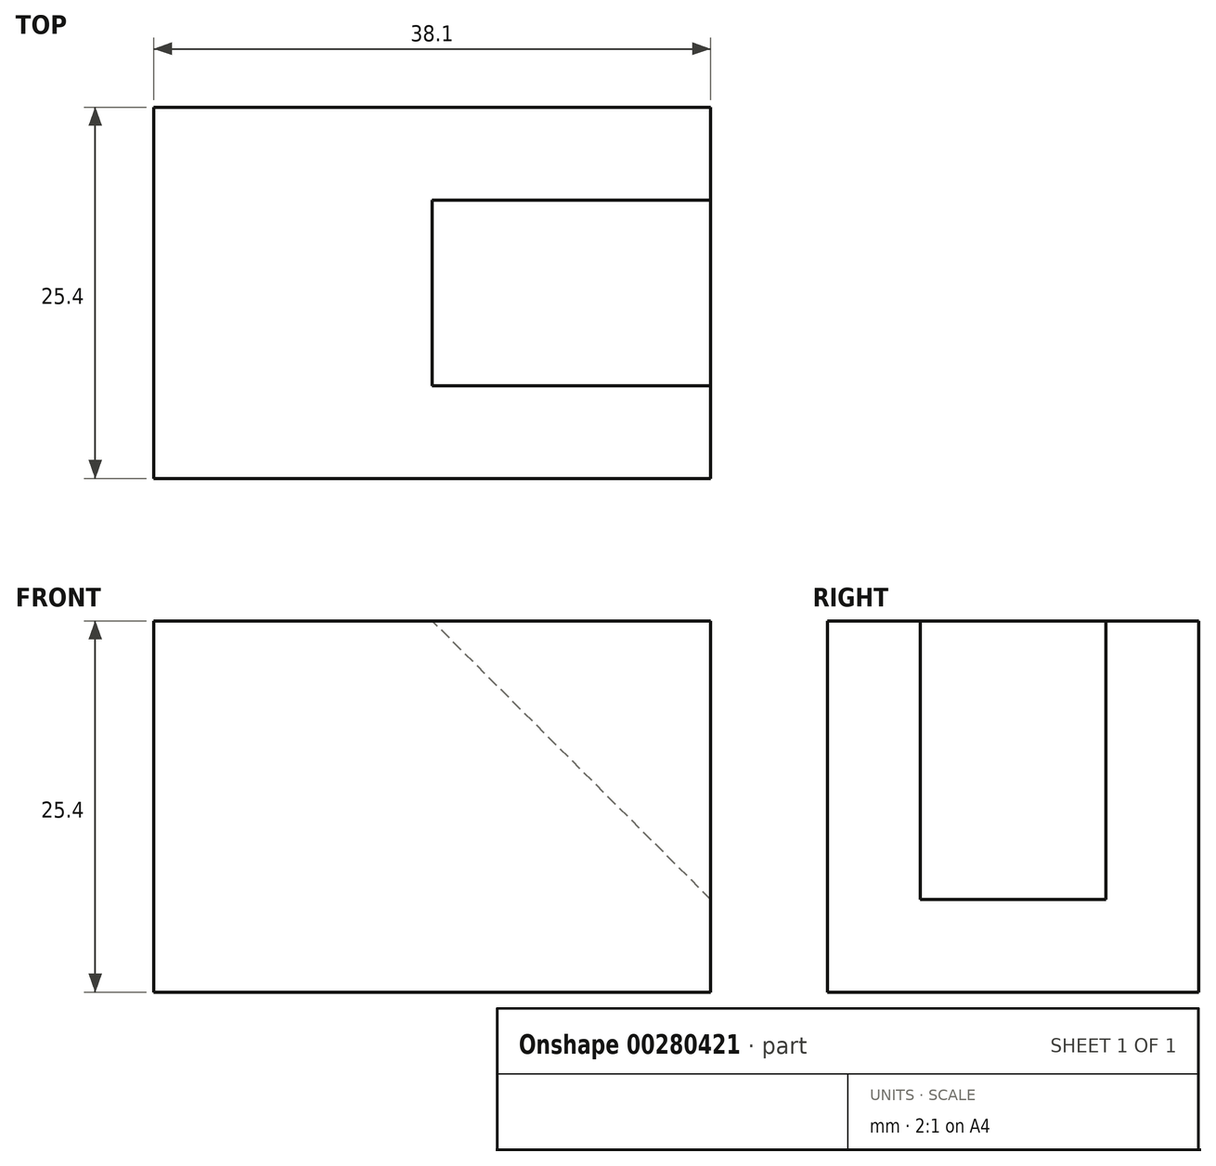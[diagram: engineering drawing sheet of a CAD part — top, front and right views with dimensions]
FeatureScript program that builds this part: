
annotation { "Feature Type Name" : "Feature", "Feature Type Description" : "" }
export const myFeature = defineFeature(function(context is Context, id is Id, definition is map)
    precondition{}
    {
        {
            var Q0;
            Q0=qCreatedBy(makeId("Front.planeOp"),FACE);
            var sketch = newSketch(context, id + "F0", { "sketchPlane" : qUnion([Q0])});
            skLineSegment(sketch, "E0.bottom", {"start": v(0, 0) * mm, "end": v(38.1, 0) * mm});
            skLineSegment(sketch, "E0.top", {"start": v(0, 25.4) * mm, "end": v(38.1, 25.4) * mm});
            skLineSegment(sketch, "E0.left", {"start": v(0, 0) * mm, "end": v(0, 25.4) * mm});
            skLineSegment(sketch, "E0.right", {"start": v(38.1, 0) * mm, "end": v(38.1, 25.4) * mm});
            skSolve(sketch);
        }
        {
            var Q0;
            Q0 = qSketchRegion(id + "F0", true);
            extrude(context, id + "F1", {"entities" : qUnion([Q0]), "depth" : 25.4 * mm, "symmetric" : true});
        }
        {
            var Q0;
            Q0=qCreatedBy(makeId("Front.planeOp"),FACE);
            var sketch = newSketch(context, id + "F2", { "sketchPlane" : qUnion([Q0])});
            skLineSegment(sketch, "E1", {"start": v(38.1, 25.4) * mm, "end": v(38.1, 6.35) * mm});
            skLineSegment(sketch, "E2", {"start": v(38.1, 6.35) * mm, "end": v(19.05, 25.4) * mm});
            skLineSegment(sketch, "E3", {"start": v(19.05, 25.4) * mm, "end": v(38.1, 25.4) * mm});
            skSolve(sketch);
        }
        {
            var Q0;
            Q0 = qSketchRegion(id + "F2", true);
            extrude(context, id + "F3", {"entities" : qUnion([Q0]), "operationType" : NewBodyOperationType.REMOVE, "oppositeDirection" : true, "depth" : 12.7 * mm, "symmetric" : true});
        }
    });
